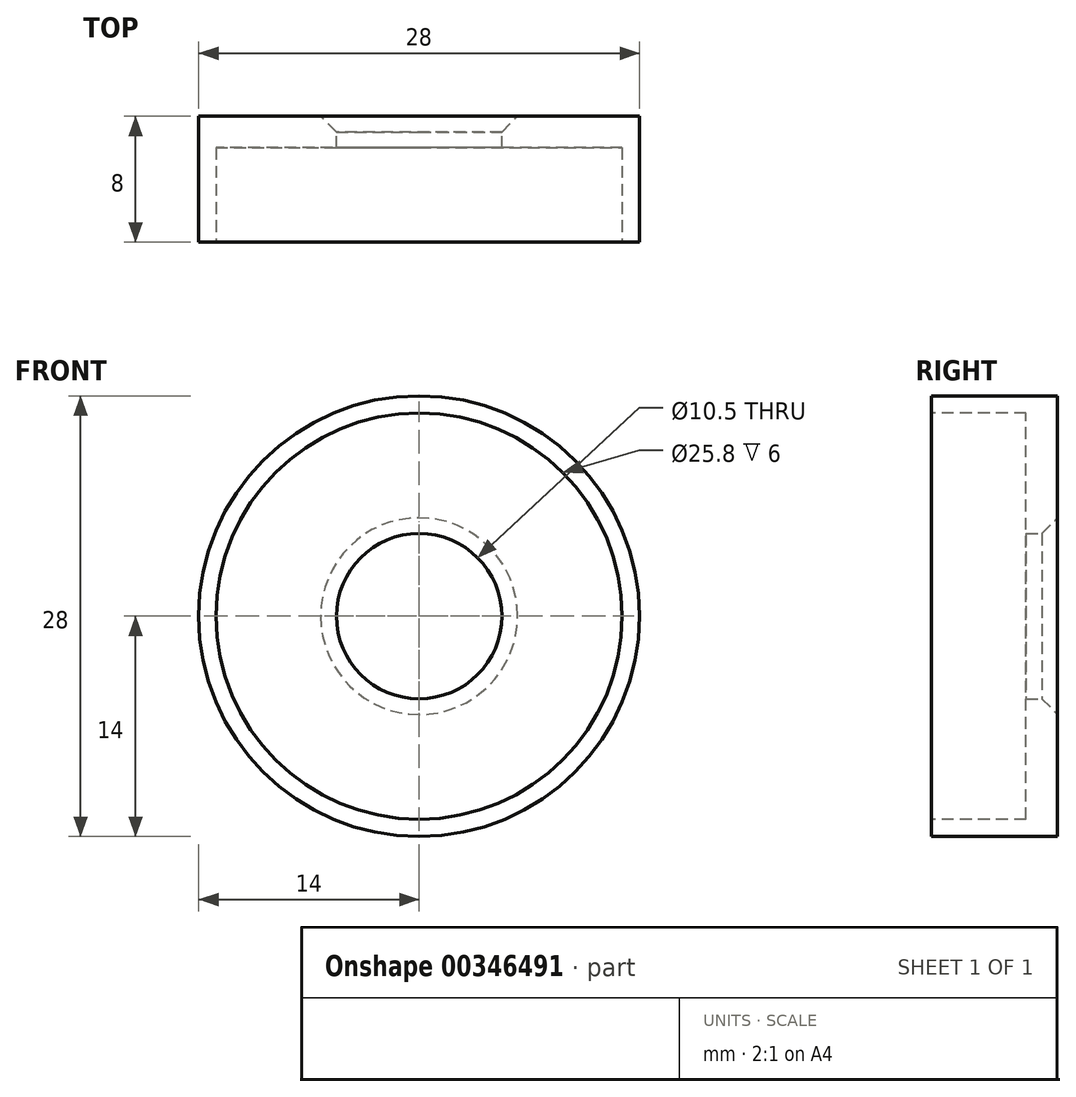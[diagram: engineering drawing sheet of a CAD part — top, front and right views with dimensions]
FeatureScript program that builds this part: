
annotation { "Feature Type Name" : "Feature", "Feature Type Description" : "" }
export const myFeature = defineFeature(function(context is Context, id is Id, definition is map)
    precondition{}
    {
        {
            var Q0;
            Q0=qCreatedBy(makeId("Top.planeOp"),FACE);
            var sketch = newSketch(context, id + "F0", { "sketchPlane" : qUnion([Q0])});
            skLineSegment(sketch, "E0", {"start": v(0, 57.22) * mm, "end": v(0, -54.71) * mm});
            skSolve(sketch);
        }
        {
            var Q0;
            Q0=qCreatedBy(makeId("Top.planeOp"),FACE);
            var sketch = newSketch(context, id + "F1", { "sketchPlane" : qUnion([Q0])});
            skLineSegment(sketch, "E1.bottom", {"start": v(5.25, 10.39) * mm, "end": v(14, 10.39) * mm});
            skLineSegment(sketch, "E1.top", {"start": v(5.25, 18.39) * mm, "end": v(14, 18.39) * mm});
            skLineSegment(sketch, "E1.left", {"start": v(5.25, 10.39) * mm, "end": v(5.25, 18.39) * mm});
            skLineSegment(sketch, "E1.right", {"start": v(14, 10.39) * mm, "end": v(14, 18.39) * mm});
            skLineSegment(sketch, "E2.bottom", {"start": v(14, 18.39) * mm, "end": v(6.4, 18.39) * mm});
            skLineSegment(sketch, "E2.top", {"start": v(14, 20.39) * mm, "end": v(6.4, 20.39) * mm});
            skLineSegment(sketch, "E2.left", {"start": v(14, 18.39) * mm, "end": v(14, 20.39) * mm});
            skLineSegment(sketch, "E2.right", {"start": v(6.4, 18.39) * mm, "end": v(6.4, 20.39) * mm});
            skSolve(sketch);
        }
        {
            var Q0;
            Q0=makeQuery(id+"F1.imprint","IMPRINT",FACE,{"disambiguationData":[TD([[makeQuery(id+"F1.imprint","IMPRINT",EDGE,{"derivedFrom":sQuery(id+"F1.wireOp",EDGE,"E2.bottom")}),-1.0]])]});
            var Q1;
            Q1=makeQuery(id+"F1.imprint","IMPRINT",FACE,{"disambiguationData":[TD([[makeQuery(id+"F1.imprint","IMPRINT",EDGE,{"derivedFrom":sQuery(id+"F1.wireOp",EDGE,"E1.bottom")}),1.0]])]});
            var Q2;
            Q2=sQuery(id+"F0.wireOp",EDGE,"E0");
            revolve(context, id + "F2", {"entities" : qUnion([Q0, Q1]), "axis" : qUnion([Q2]), "revolveType" : RevolveType.FULL});
        }
        {
            var Q0;
            Q0=makeQuery(id+"F2.opRevolve","SWEPT_FACE",FACE,{"disambiguationData":[OSD([sQuery(id+"F1.wireOp",EDGE,"E1.bottom")])]});
            var sketch = newSketch(context, id + "F3", { "sketchPlane" : qUnion([Q0])});
            skCircle(sketch, "E3", {"center": v(0, 0) * mm, "radius": 12.9 * mm});
            skSolve(sketch);
        }
        {
            var Q0;
            Q0=makeQuery(id+"F3.imprint","IMPRINT",FACE,{"disambiguationData":[TD([[makeQuery(id+"F3.imprint","IMPRINT",EDGE,{"derivedFrom":sQuery(id+"F3.wireOp",EDGE,"E3")}),1.0]])]});
            extrude(context, id + "F4", {"entities" : qUnion([Q0]), "operationType" : NewBodyOperationType.REMOVE, "oppositeDirection" : true, "depth" : 6 * mm});
        }
        {
            var Q0;
            Q0=makeQuery(id+"F2.opRevolve","SWEPT_EDGE",EDGE,{"disambiguationData":[OSD([sQuery(id+"F1.wireOp",EDGE,"E1.top"),sQuery(id+"F1.wireOp",EDGE,"E1.left")])]});
            chamfer(context, id + "F5", {"entities" : qUnion([Q0]), "width" : 1 * mm, "tangentPropagation" : true});
        }
    });
